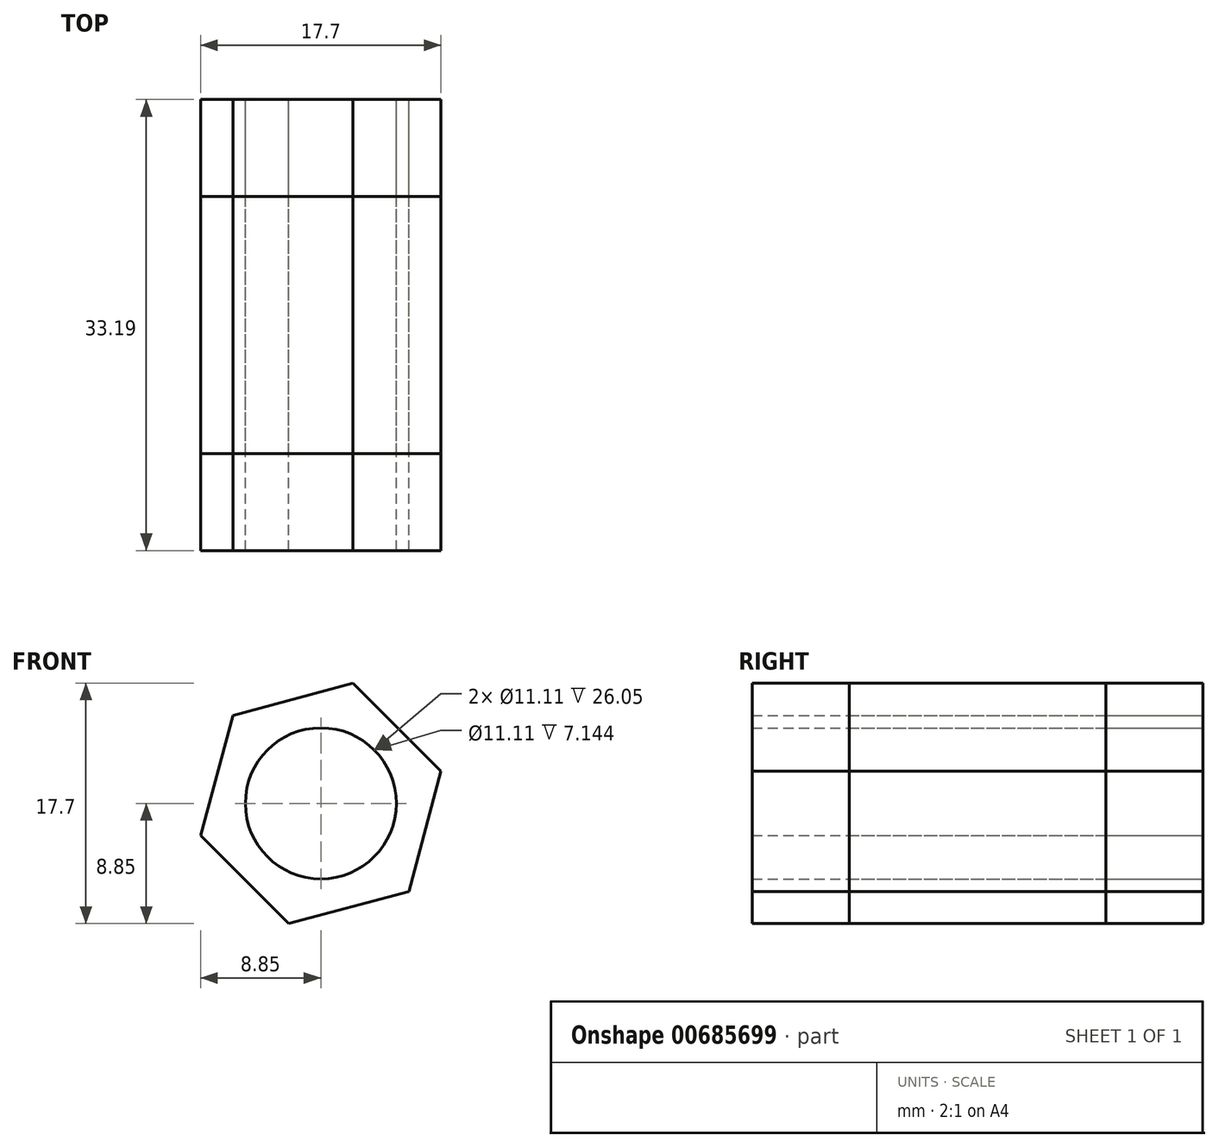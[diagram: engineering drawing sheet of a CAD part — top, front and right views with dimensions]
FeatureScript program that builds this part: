
annotation { "Feature Type Name" : "Feature", "Feature Type Description" : "" }
export const myFeature = defineFeature(function(context is Context, id is Id, definition is map)
    precondition{}
    {
        {
            var Q0;
            Q0=qCreatedBy(makeId("Front.planeOp"),FACE);
            var sketch = newSketch(context, id + "F0", { "sketchPlane" : qUnion([Q0])});
            skCircle(sketch, "E0.cCircle", {"center": v(0, 0) * mm, "radius": 7.94 * mm, "construction": true});
            skLineSegment(sketch, "E0.0", {"start": v(2.37, 8.85) * mm, "end": v(8.85, 2.37) * mm});
            skLineSegment(sketch, "E0.1", {"start": v(8.85, 2.37) * mm, "end": v(6.48, -6.48) * mm});
            skLineSegment(sketch, "E0.2", {"start": v(6.48, -6.48) * mm, "end": v(-2.37, -8.85) * mm});
            skLineSegment(sketch, "E0.3", {"start": v(-2.37, -8.85) * mm, "end": v(-8.85, -2.37) * mm});
            skLineSegment(sketch, "E0.4", {"start": v(-8.85, -2.37) * mm, "end": v(-6.48, 6.48) * mm});
            skLineSegment(sketch, "E0.5", {"start": v(-6.48, 6.48) * mm, "end": v(2.37, 8.85) * mm});
            skPoint(sketch, "E0.0.midPoint", {"position": v(5.61, 5.61) * mm});
            skCircle(sketch, "E1", {"center": v(0, 0) * mm, "radius": 5.56 * mm});
            skSolve(sketch);
        }
        {
            var Q0;
            Q0=makeQuery(id+"F0.imprint","IMPRINT",FACE,{"disambiguationData":[TD([[makeQuery(id+"F0.imprint","IMPRINT",EDGE,{"derivedFrom":sQuery(id+"F0.wireOp",EDGE,"E0.0")}),-1.0]])]});
            extrude(context, id + "F1", {"entities" : qUnion([Q0]), "depth" : 7.14 * mm, "offsetDistance" : 25.4 * mm});
        }
        {
            var Q0;
            Q0 = qSketchRegion(id + "F0", true);
            var Q1;
            Q1=makeQuery(id+"F1.opExtrude","CAP_FACE",FACE,{"disambiguationData":[OSD([sQuery(id+"F0.wireOp",EDGE,"E0.0"),sQuery(id+"F0.wireOp",EDGE,"E0.1"),sQuery(id+"F0.wireOp",EDGE,"E0.2"),sQuery(id+"F0.wireOp",EDGE,"E0.3"),sQuery(id+"F0.wireOp",EDGE,"E0.4"),sQuery(id+"F0.wireOp",EDGE,"E0.5"),sQuery(id+"F0.wireOp",EDGE,"E1")])],"isStart":false});
            extrude(context, id + "F2", {"entities" : qUnion([Q0, Q1]), "endBound" : BoundingType.THROUGH_ALL, "depth" : 25.4 * mm, "offsetDistance" : 25.4 * mm});
        }
    });
